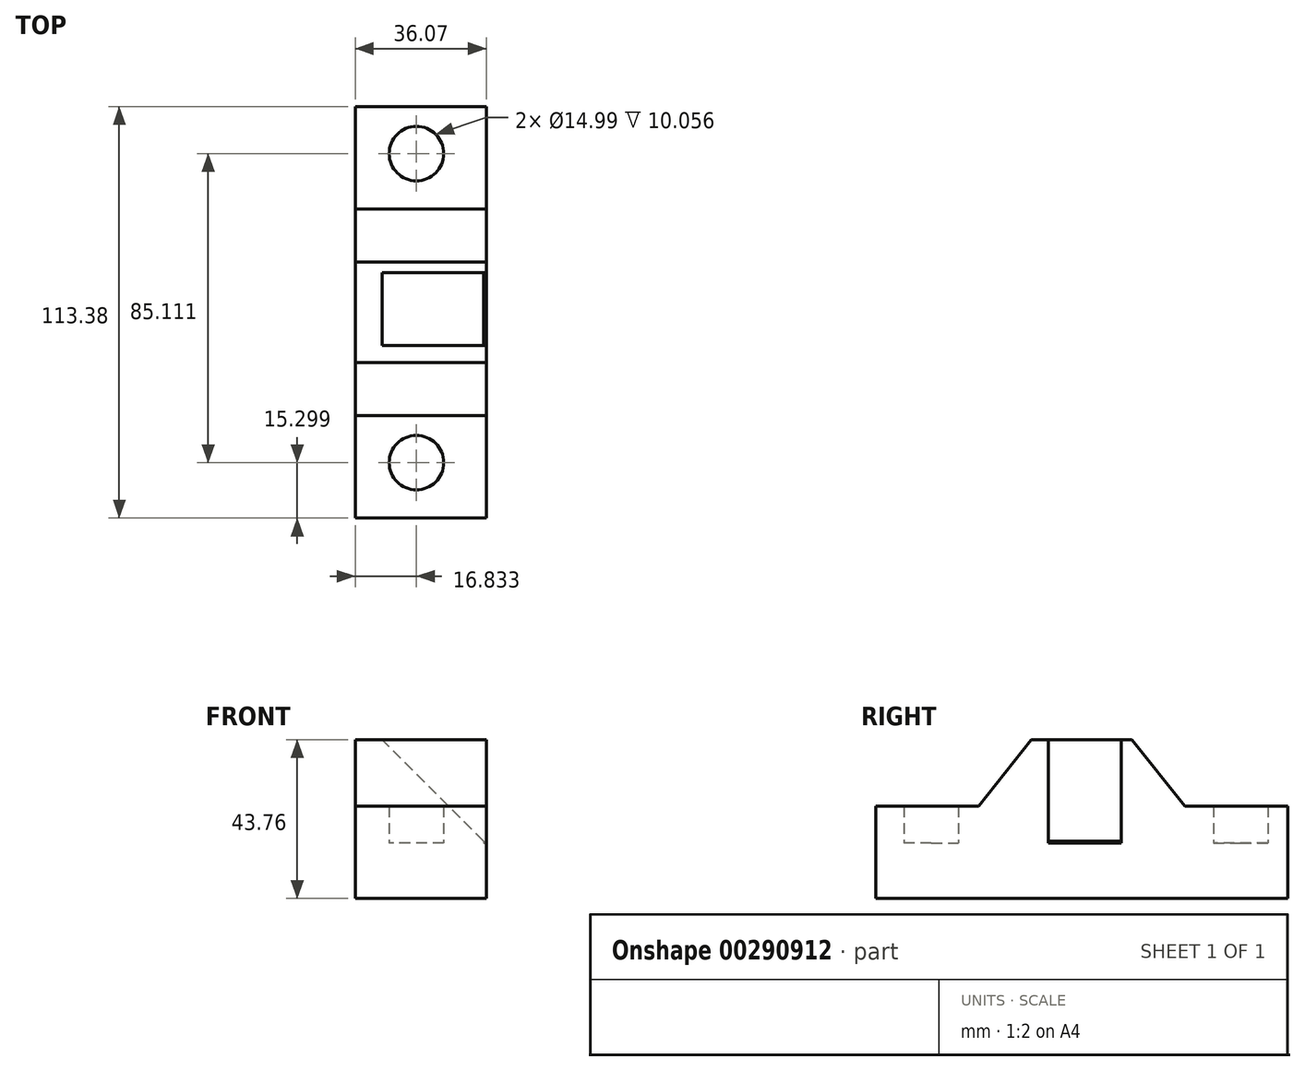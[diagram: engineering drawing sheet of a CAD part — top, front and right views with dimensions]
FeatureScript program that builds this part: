
annotation { "Feature Type Name" : "Feature", "Feature Type Description" : "" }
export const myFeature = defineFeature(function(context is Context, id is Id, definition is map)
    precondition{}
    {
        {
            var Q0;
            Q0=qCreatedBy(makeId("Right.planeOp"),FACE);
            var sketch = newSketch(context, id + "F0", { "sketchPlane" : qUnion([Q0])});
            skLineSegment(sketch, "E0", {"start": v(-63.83, 10.06) * mm, "end": v(-35.56, 10.06) * mm});
            skLineSegment(sketch, "E1", {"start": v(-35.56, 10.06) * mm, "end": v(-63.83, 10.06) * mm});
            skLineSegment(sketch, "E2", {"start": v(-63.83, -15.34) * mm, "end": v(-63.83, 10.06) * mm});
            skLineSegment(sketch, "E3", {"start": v(-63.83, -15.34) * mm, "end": v(49.55, -15.34) * mm});
            skLineSegment(sketch, "E4", {"start": v(49.55, -15.34) * mm, "end": v(49.55, 10.06) * mm});
            skLineSegment(sketch, "E5", {"start": v(49.55, 10.06) * mm, "end": v(21.28, 10.06) * mm});
            skLineSegment(sketch, "E6", {"start": v(21.28, 10.06) * mm, "end": v(6.7, 28.42) * mm});
            skLineSegment(sketch, "E7", {"start": v(6.7, 28.42) * mm, "end": v(6.7, 10.06) * mm});
            skLineSegment(sketch, "E8", {"start": v(-35.56, 10.06) * mm, "end": v(-20.99, 28.42) * mm});
            skLineSegment(sketch, "E9", {"start": v(-20.99, 28.42) * mm, "end": v(-20.99, 10.06) * mm});
            skLineSegment(sketch, "E10", {"start": v(-20.99, 10.06) * mm, "end": v(6.7, 10.06) * mm});
            skLineSegment(sketch, "E11", {"start": v(6.7, 28.42) * mm, "end": v(-20.99, 28.42) * mm});
            skSolve(sketch);
        }
        {
            var Q0;
            Q0 = qSketchRegion(id + "F0", true);
            extrude(context, id + "F1", {"entities" : qUnion([Q0]), "oppositeDirection" : true, "depth" : 36.07 * mm});
        }
        {
            var Q0;
            Q0=qCreatedBy(makeId("Top.planeOp"),FACE);
            var sketch = newSketch(context, id + "F2", { "sketchPlane" : qUnion([Q0])});
            skCircle(sketch, "E12", {"center": v(-19.24, -48.53) * mm, "radius": 7.5 * mm});
            skCircle(sketch, "E13", {"center": v(-19.24, 36.58) * mm, "radius": 7.5 * mm});
            skSolve(sketch);
        }
        {
            var Q0;
            Q0 = qSketchRegion(id + "F2", true);
            extrude(context, id + "F3", {"entities" : qUnion([Q0]), "operationType" : NewBodyOperationType.REMOVE, "depth" : 57.4 * mm});
        }
        {
            var Q0;
            Q0=qCreatedBy(makeId("Right.planeOp"),FACE);
            var sketch = newSketch(context, id + "F4", { "sketchPlane" : qUnion([Q0])});
            skLineSegment(sketch, "E14.bottom", {"start": v(3.79, 29) * mm, "end": v(-16.32, 29) * mm});
            skLineSegment(sketch, "E14.top", {"start": v(3.79, 0) * mm, "end": v(-16.32, 0) * mm});
            skLineSegment(sketch, "E14.left", {"start": v(3.79, 29) * mm, "end": v(3.79, 0) * mm});
            skLineSegment(sketch, "E14.right", {"start": v(-16.32, 29) * mm, "end": v(-16.32, 0) * mm});
            skSolve(sketch);
        }
        {
            var Q0;
            Q0 = qSketchRegion(id + "F4", true);
            extrude(context, id + "F5", {"entities" : qUnion([Q0]), "operationType" : NewBodyOperationType.REMOVE, "oppositeDirection" : true, "depth" : 0.76 * mm});
        }
        {
            var Q0;
            Q0=makeQuery(id+"F5.boolean.opBoolean","INTERSECT",EDGE,{"derivedFrom":[makeQuery(id+"F1.opExtrude","SWEPT_FACE",FACE,{"disambiguationData":[OSD([sQuery(id+"F0.wireOp",EDGE,"E11")])]}),makeQuery(id+"F5.opExtrude","CAP_FACE",FACE,{"disambiguationData":[OSD([sQuery(id+"F4.wireOp",EDGE,"E14.bottom"),sQuery(id+"F4.wireOp",EDGE,"E14.top"),sQuery(id+"F4.wireOp",EDGE,"E14.left"),sQuery(id+"F4.wireOp",EDGE,"E14.right")])],"isStart":false})]});
            chamfer(context, id + "F6", {"entities" : qUnion([Q0]), "width" : 27.94 * mm, "tangentPropagation" : true});
        }
    });
